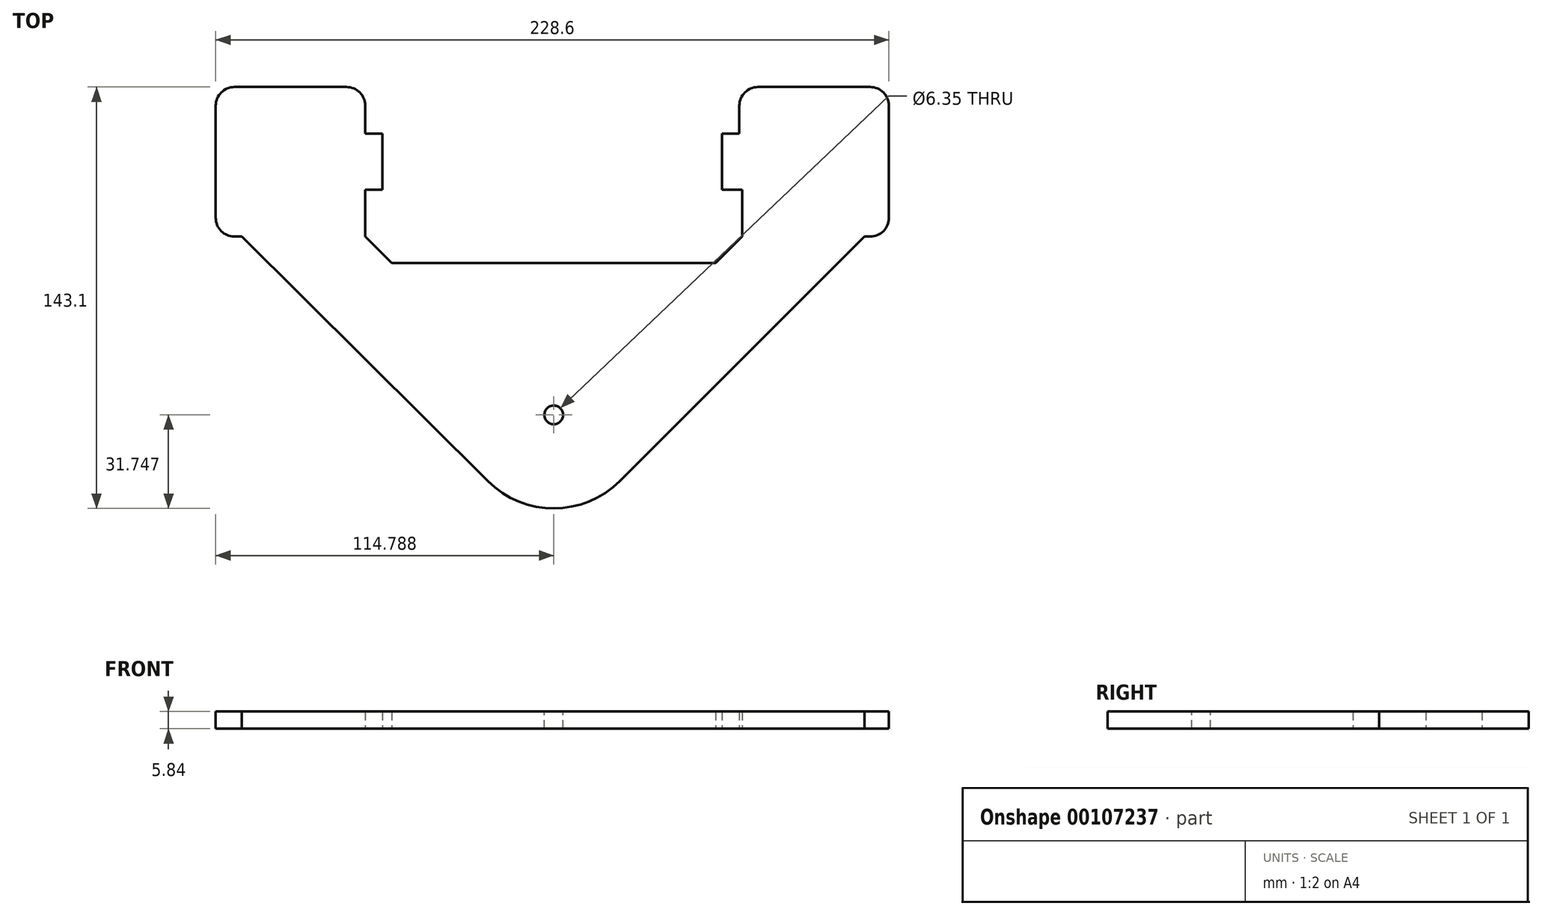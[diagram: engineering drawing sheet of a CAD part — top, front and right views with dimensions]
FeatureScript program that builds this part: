
annotation { "Feature Type Name" : "Feature", "Feature Type Description" : "" }
export const myFeature = defineFeature(function(context is Context, id is Id, definition is map)
    precondition{}
    {
        {
            var Q0;
            Q0=qCreatedBy(makeId("Top.planeOp"),FACE);
            var sketch = newSketch(context, id + "F0", { "sketchPlane" : qUnion([Q0])});
            skLineSegment(sketch, "E0", {"start": v(-43.46, 15.87) * mm, "end": v(-37.1, 15.87) * mm});
            skLineSegment(sketch, "E1", {"start": v(-30.76, 9.52) * mm, "end": v(-30.76, 0) * mm});
            skLineSegment(sketch, "E2", {"start": v(-30.76, 0) * mm, "end": v(-24.92, 0) * mm});
            skLineSegment(sketch, "E3", {"start": v(-24.92, 0) * mm, "end": v(-24.92, -19.05) * mm});
            skLineSegment(sketch, "E4", {"start": v(-24.92, -19.05) * mm, "end": v(-30.76, -19.05) * mm});
            skLineSegment(sketch, "E5", {"start": v(-30.76, -19.05) * mm, "end": v(-30.76, -34.92) * mm});
            skLineSegment(sketch, "E6", {"start": v(90.4, 0) * mm, "end": v(96.24, 0) * mm});
            skLineSegment(sketch, "E7", {"start": v(96.24, 0) * mm, "end": v(96.24, 9.52) * mm});
            skLineSegment(sketch, "E8", {"start": v(102.6, 15.88) * mm, "end": v(108.94, 15.88) * mm});
            skLineSegment(sketch, "E9", {"start": v(97.21, -34.92) * mm, "end": v(97.21, -19.05) * mm});
            skLineSegment(sketch, "E10", {"start": v(97.21, -19.05) * mm, "end": v(90.4, -19.05) * mm});
            skLineSegment(sketch, "E11", {"start": v(90.4, -19.05) * mm, "end": v(90.4, 0) * mm});
            skLineSegment(sketch, "E12", {"start": v(-30.76, -34.93) * mm, "end": v(-21.78, -43.9) * mm});
            skLineSegment(sketch, "E13", {"start": v(-21.78, -43.9) * mm, "end": v(88.23, -43.9) * mm});
            skLineSegment(sketch, "E14", {"start": v(88.23, -43.9) * mm, "end": v(97.21, -34.92) * mm});
            skCircle(sketch, "E15", {"center": v(33.23, -95.47) * mm, "radius": 31.75 * mm});
            skLineSegment(sketch, "E16", {"start": v(-56.74, -50.8) * mm, "end": v(10.84, -117.99) * mm});
            skLineSegment(sketch, "E17", {"start": v(55.68, -117.92) * mm, "end": v(110.94, -62.66) * mm});
            skLineSegment(sketch, "E18", {"start": v(-43.46, 15.87) * mm, "end": v(-75.2, 15.87) * mm});
            skLineSegment(sketch, "E19", {"start": v(-81.56, 9.52) * mm, "end": v(-81.56, -28.58) * mm});
            skLineSegment(sketch, "E20", {"start": v(-56.74, -50.8) * mm, "end": v(-72.71, -34.93) * mm});
            skPoint(sketch, "E21", {"position": v(33.23, -43.9) * mm});
            skLineSegment(sketch, "E22", {"start": v(-72.71, -34.93) * mm, "end": v(-75.2, -34.93) * mm});
            skLineSegment(sketch, "E23", {"start": v(108.94, 15.88) * mm, "end": v(140.7, 15.88) * mm});
            skLineSegment(sketch, "E24", {"start": v(110.94, -62.66) * mm, "end": v(138.68, -34.92) * mm});
            skLineSegment(sketch, "E25", {"start": v(147.04, 9.53) * mm, "end": v(147.04, -28.57) * mm});
            skLineSegment(sketch, "E26", {"start": v(138.68, -34.92) * mm, "end": v(140.7, -34.92) * mm});
            skPoint(sketch, "E27.visualSharp", {"position": v(-81.56, 15.87) * mm});
            skArc(sketch, "E27.filletArc", {"start": v(-75.2, 15.87) * mm, "mid": v(-79.7, 14.02) * mm, "end": v(-81.56, 9.52) * mm});
            skPoint(sketch, "E28.visualSharp", {"position": v(-81.56, -34.93) * mm});
            skArc(sketch, "E28.filletArc", {"start": v(-81.56, -28.58) * mm, "mid": v(-79.7, -33.07) * mm, "end": v(-75.2, -34.93) * mm});
            skPoint(sketch, "E29.visualSharp", {"position": v(147.04, -34.92) * mm});
            skArc(sketch, "E29.filletArc", {"start": v(140.7, -34.92) * mm, "mid": v(145.18, -33.06) * mm, "end": v(147.04, -28.57) * mm});
            skPoint(sketch, "E30.visualSharp", {"position": v(147.04, 15.88) * mm});
            skArc(sketch, "E30.filletArc", {"start": v(147.04, 9.53) * mm, "mid": v(145.18, 14.02) * mm, "end": v(140.7, 15.88) * mm});
            skPoint(sketch, "E31.visualSharp", {"position": v(96.24, 15.87) * mm});
            skArc(sketch, "E31.filletArc", {"start": v(102.6, 15.88) * mm, "mid": v(98.1, 14.02) * mm, "end": v(96.24, 9.52) * mm});
            skPoint(sketch, "E32.visualSharp", {"position": v(-30.76, 15.87) * mm});
            skArc(sketch, "E32.filletArc", {"start": v(-30.76, 9.52) * mm, "mid": v(-32.62, 14.02) * mm, "end": v(-37.1, 15.87) * mm});
            skPoint(sketch, "E33", {"position": v(33.23, -127.22) * mm});
            skPoint(sketch, "E34", {"position": v(-24.92, -9.53) * mm});
            skSolve(sketch);
        }
        {
            var Q0;
            Q0=makeQuery(id+"F0.imprint","IMPRINT",FACE,{"disambiguationData":[TD([[makeQuery(id+"F0.imprint","IMPRINT",EDGE,{"derivedFrom":sQuery(id+"F0.wireOp",EDGE,"E0")}),-1.0]])]});
            var Q1;
            Q1=makeQuery(id+"F0.imprint","IMPRINT",FACE,{"disambiguationData":[TD([[makeQuery(id+"F0.imprint","IMPRINT",EDGE,{"derivedFrom":sQuery(id+"F0.wireOp",EDGE,"T5kYt2XQ-MBXw-SNko-ycwS-8WTvdcoaHxM5")}),-1.0]])]});
            var Q2;
            Q2=makeQuery(id+"F0.imprint","IMPRINT",FACE,{"disambiguationData":[TD([[makeQuery(id+"F0.imprint","IMPRINT",EDGE,{"derivedFrom":sQuery(id+"F0.wireOp",EDGE,"E6")}),-1.0]])]});
            var Q3;
            {var subQ0=sQuery(id+"F0.wireOp",EDGE,"lhIs2V5k-124r-XnZm-OG7W-aaeC0uC0tlui");Q3=makeQuery(id+"F0.imprint","IMPRINT",FACE,{"disambiguationData":[TD([[makeQuery(id+"F0.imprint","IMPRINT",EDGE,{"derivedFrom":subQ0}),-1.0]])]});}
            var Q4;
            {var subQ0=sQuery(id+"F0.wireOp",EDGE,"lhIs2V5k-124r-XnZm-OG7W-aaeC0uC0tlui");Q4=makeQuery(id+"F0.imprint","IMPRINT",FACE,{"disambiguationData":[TD([[makeQuery(id+"F0.imprint","IMPRINT",EDGE,{"derivedFrom":subQ0}),1.0]])]});}
            var Q5;
            Q5=makeQuery(id+"F0.imprint","IMPRINT",FACE,{"disambiguationData":[TD([[makeQuery(id+"F0.imprint","IMPRINT",EDGE,{"derivedFrom":sQuery(id+"F0.wireOp",EDGE,"rerKqeod-Ae5W-xU64-WBFC-FY7INiN1wkvI")}),-1.0]])]});
            var Q6;
            Q6=makeQuery(id+"F0.imprint","IMPRINT",FACE,{"disambiguationData":[TD([[makeQuery(id+"F0.imprint","IMPRINT",EDGE,{"derivedFrom":sQuery(id+"F0.wireOp",EDGE,"iHk6zPM7-oFqR-BrBY-6vQg-eick85NQ3Ttv")}),1.0]])]});
            var Q7;
            {var subQ0=sQuery(id+"F0.wireOp",EDGE,"E15");var subQ1=makeQuery(id+"F0.imprint","INTERSECT",VERTEX,{"derivedFrom":[subQ0,sQuery(id+"F0.wireOp",EDGE,"E16")]});Q7=makeQuery(id+"F0.imprint","IMPRINT",FACE,{"disambiguationData":[TD([[makeQuery(id+"F0.imprint","IMPRINT",EDGE,{"disambiguationData":[TD([[subQ1,-1.0]])],"derivedFrom":subQ0}),1.0]])]});}
            extrude(context, id + "F1", {"entities" : qUnion([Q0, Q1, Q2, Q3, Q4, Q5, Q6, Q7]), "depth" : 5.84 * mm});
        }
        {
            var Q0;
            Q0=makeQuery(id+"F1.opExtrude","CAP_FACE",FACE,{"disambiguationData":[OSD([sQuery(id+"F0.wireOp",EDGE,"E0"),sQuery(id+"F0.wireOp",EDGE,"E1"),sQuery(id+"F0.wireOp",EDGE,"E2"),sQuery(id+"F0.wireOp",EDGE,"E3"),sQuery(id+"F0.wireOp",EDGE,"E4"),sQuery(id+"F0.wireOp",EDGE,"E5"),sQuery(id+"F0.wireOp",EDGE,"rerKqeod-Ae5W-xU64-WBFC-FY7INiN1wkvI"),sQuery(id+"F0.wireOp",EDGE,"E6"),sQuery(id+"F0.wireOp",EDGE,"E7"),sQuery(id+"F0.wireOp",EDGE,"E8"),sQuery(id+"F0.wireOp",EDGE,"iHk6zPM7-oFqR-BrBY-6vQg-eick85NQ3Ttv"),sQuery(id+"F0.wireOp",EDGE,"E9"),sQuery(id+"F0.wireOp",EDGE,"E10"),sQuery(id+"F0.wireOp",EDGE,"E11"),sQuery(id+"F0.wireOp",EDGE,"E12"),sQuery(id+"F0.wireOp",EDGE,"E13"),sQuery(id+"F0.wireOp",EDGE,"E14"),sQuery(id+"F0.wireOp",EDGE,"hR697QTB-tOrR-csCD-HdAD-kju1jfNnlCUA"),sQuery(id+"F0.wireOp",EDGE,"phjMm00T-TaJB-ipjm-NTRG-nsfIap735zAD"),sQuery(id+"F0.wireOp",EDGE,"0hCXLiCt-i7vr-U8HS-u4SZ-Qfzw9ioVZAWG"),sQuery(id+"F0.wireOp",EDGE,"MAWq8pZc-r6kU-yDQy-BJ7a-H4aixHtaey74"),sQuery(id+"F0.wireOp",EDGE,"QCKpwlB1-kboF-oJfI-24mF-nmhR9O9CBc1U"),sQuery(id+"F0.wireOp",EDGE,"DnfC9uw0-OS6o-0w9a-LkZ6-V9UKZb0FaXwd"),sQuery(id+"F0.wireOp",EDGE,"E15")])],"isStart":false});
            var sketch = newSketch(context, id + "F2", { "sketchPlane" : qUnion([Q0])});
            skCircle(sketch, "E35", {"center": v(33.23, -95.47) * mm, "radius": 3.17 * mm});
            skSolve(sketch);
        }
        {
            var Q0;
            Q0=makeQuery(id+"F2.imprint","IMPRINT",FACE,{"disambiguationData":[TD([[makeQuery(id+"F2.imprint","IMPRINT",EDGE,{"derivedFrom":sQuery(id+"F2.wireOp",EDGE,"E35")}),1.0]])]});
            var Q1;
            Q1=makeQuery(id+"F1.opExtrude","CAP_FACE",FACE,{"disambiguationData":[OSD([sQuery(id+"F0.wireOp",EDGE,"E0"),sQuery(id+"F0.wireOp",EDGE,"E1"),sQuery(id+"F0.wireOp",EDGE,"E2"),sQuery(id+"F0.wireOp",EDGE,"E3"),sQuery(id+"F0.wireOp",EDGE,"E4"),sQuery(id+"F0.wireOp",EDGE,"E5"),sQuery(id+"F0.wireOp",EDGE,"rerKqeod-Ae5W-xU64-WBFC-FY7INiN1wkvI"),sQuery(id+"F0.wireOp",EDGE,"E6"),sQuery(id+"F0.wireOp",EDGE,"E7"),sQuery(id+"F0.wireOp",EDGE,"E8"),sQuery(id+"F0.wireOp",EDGE,"iHk6zPM7-oFqR-BrBY-6vQg-eick85NQ3Ttv"),sQuery(id+"F0.wireOp",EDGE,"E9"),sQuery(id+"F0.wireOp",EDGE,"E10"),sQuery(id+"F0.wireOp",EDGE,"E11"),sQuery(id+"F0.wireOp",EDGE,"E12"),sQuery(id+"F0.wireOp",EDGE,"E13"),sQuery(id+"F0.wireOp",EDGE,"E14"),sQuery(id+"F0.wireOp",EDGE,"hR697QTB-tOrR-csCD-HdAD-kju1jfNnlCUA"),sQuery(id+"F0.wireOp",EDGE,"phjMm00T-TaJB-ipjm-NTRG-nsfIap735zAD"),sQuery(id+"F0.wireOp",EDGE,"0hCXLiCt-i7vr-U8HS-u4SZ-Qfzw9ioVZAWG"),sQuery(id+"F0.wireOp",EDGE,"MAWq8pZc-r6kU-yDQy-BJ7a-H4aixHtaey74"),sQuery(id+"F0.wireOp",EDGE,"QCKpwlB1-kboF-oJfI-24mF-nmhR9O9CBc1U"),sQuery(id+"F0.wireOp",EDGE,"DnfC9uw0-OS6o-0w9a-LkZ6-V9UKZb0FaXwd"),sQuery(id+"F0.wireOp",EDGE,"E15")])],"isStart":true});
            extrude(context, id + "F3", {"entities" : qUnion([Q0]), "operationType" : NewBodyOperationType.REMOVE, "endBound" : BoundingType.UP_TO_SURFACE, "oppositeDirection" : true, "endBoundEntityFace" : qUnion([Q1]), "depth" : 25.4 * mm});
        }
    });
